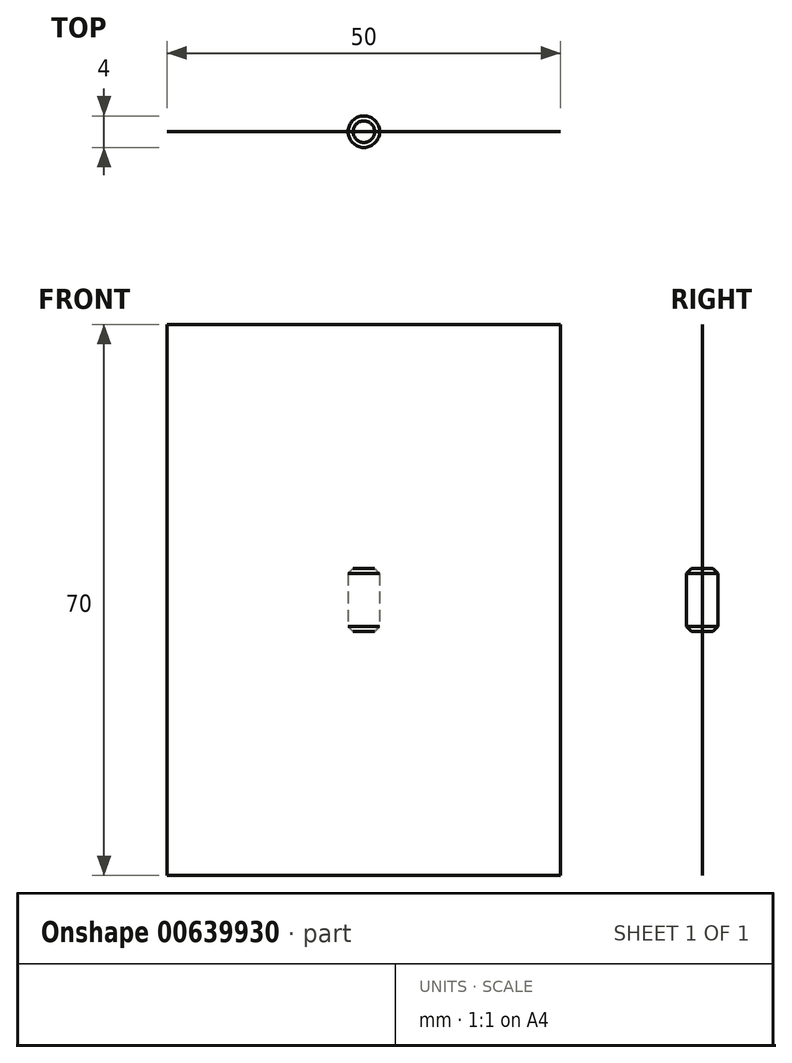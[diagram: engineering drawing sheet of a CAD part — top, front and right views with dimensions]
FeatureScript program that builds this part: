
annotation { "Feature Type Name" : "Feature", "Feature Type Description" : "" }
export const myFeature = defineFeature(function(context is Context, id is Id, definition is map)
    precondition{}
    {
        {
            var Q0;
            Q0=qCreatedBy(makeId("Top.planeOp"),FACE);
            var sketch = newSketch(context, id + "F0", { "sketchPlane" : qUnion([Q0])});
            skCircle(sketch, "E0", {"center": v(0, 0) * mm, "radius": 2 * mm});
            skSolve(sketch);
        }
        {
            var Q0;
            Q0 = qSketchRegion(id + "F0", true);
            extrude(context, id + "F1", {"entities" : qUnion([Q0]), "depth" : 8 * mm, "offsetDistance" : 25 * mm, "symmetric" : true});
        }
        {
            var Q0;
            Q0=makeQuery(id+"F1.opExtrude","CAP_EDGE",EDGE,{"disambiguationData":[OSD([sQuery(id+"F0.wireOp",EDGE,"E0")])],"isStart":false});
            var Q1;
            Q1=makeQuery(id+"F1.opExtrude","CAP_EDGE",EDGE,{"disambiguationData":[OSD([sQuery(id+"F0.wireOp",EDGE,"E0")])],"isStart":true});
            chamfer(context, id + "F2", {"entities" : qUnion([Q0, Q1]), "width" : 0.63 * mm, "tangentPropagation" : true});
        }
        {
            var Q0;
            Q0=qCreatedBy(makeId("Front.planeOp"),FACE);
            var sketch = newSketch(context, id + "F3", { "sketchPlane" : qUnion([Q0])});
            skLineSegment(sketch, "E1.bottom", {"start": v(25, -35) * mm, "end": v(-25, -35) * mm});
            skLineSegment(sketch, "E1.top", {"start": v(25, 35) * mm, "end": v(-25, 35) * mm});
            skLineSegment(sketch, "E1.left", {"start": v(25, -35) * mm, "end": v(25, 35) * mm});
            skLineSegment(sketch, "E1.right", {"start": v(-25, -35) * mm, "end": v(-25, 35) * mm});
            skPoint(sketch, "E1.middle", {"position": v(0, 0) * mm});
            skSolve(sketch);
        }
        {
            var Q0;
            Q0 = qSketchRegion(id + "F3", true);
            extrude(context, id + "F4", {"entities" : qUnion([Q0]), "depth" : 1 / 406.4 * mm, "offsetDistance" : 25 * mm});
        }
    });
